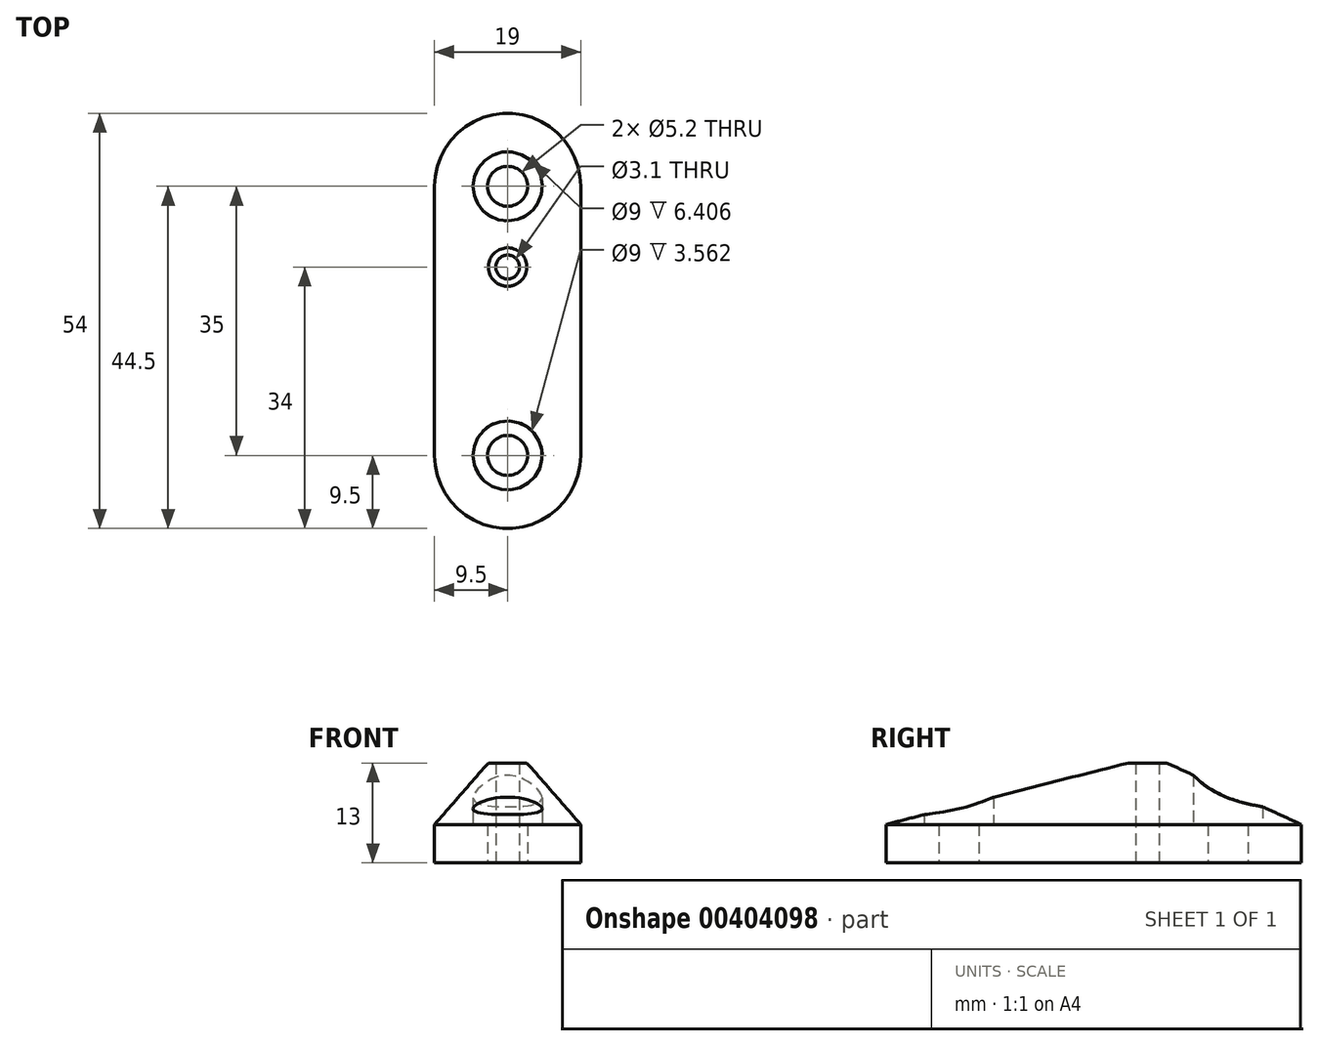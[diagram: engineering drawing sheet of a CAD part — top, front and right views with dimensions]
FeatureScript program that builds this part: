
annotation { "Feature Type Name" : "Feature", "Feature Type Description" : "" }
export const myFeature = defineFeature(function(context is Context, id is Id, definition is map)
    precondition{}
    {
        {
            var Q0;
            Q0=qCreatedBy(makeId("Top.planeOp"),FACE);
            var sketch = newSketch(context, id + "F0", { "sketchPlane" : qUnion([Q0])});
            skArc(sketch, "E0", {"start": v(9.5, 20) * mm, "mid": v(0, 29.5) * mm, "end": v(-9.5, 20) * mm});
            skArc(sketch, "E1", {"start": v(-9.5, -15) * mm, "mid": v(0, -24.5) * mm, "end": v(9.5, -15) * mm});
            skLineSegment(sketch, "E2", {"start": v(-9.5, 20) * mm, "end": v(-9.5, -15) * mm});
            skLineSegment(sketch, "E3", {"start": v(9.5, 20) * mm, "end": v(9.5, -15) * mm});
            skSolve(sketch);
        }
        {
            var Q0;
            Q0=makeQuery(id+"F0.imprint","IMPRINT",FACE,{"disambiguationData":[TD([[makeQuery(id+"F0.imprint","IMPRINT",EDGE,{"derivedFrom":sQuery(id+"F0.wireOp",EDGE,"E0")}),1.0]])]});
            extrude(context, id + "F1", {"entities" : qUnion([Q0]), "depth" : 5 * mm});
        }
        {
            var Q0;
            Q0=makeQuery(id+"F1.opExtrude","CAP_FACE",FACE,{"disambiguationData":[OSD([sQuery(id+"F0.wireOp",EDGE,"E0"),sQuery(id+"F0.wireOp",EDGE,"E1"),sQuery(id+"F0.wireOp",EDGE,"E2"),sQuery(id+"F0.wireOp",EDGE,"E3")])],"isStart":false});
            var sketch = newSketch(context, id + "F2", { "sketchPlane" : qUnion([Q0])});
            skCircle(sketch, "E4", {"center": v(0, -15) * mm, "radius": 4.5 * mm});
            skCircle(sketch, "E5", {"center": v(0, 20) * mm, "radius": 4.5 * mm});
            skSolve(sketch);
        }
        {
            var Q0;
            Q0=qCreatedBy(makeId("Top.planeOp"),FACE);
            cPlane(context, id + "F3", {"entities" : qUnion([Q0]), "cplaneType" : CPlaneType.OFFSET, "offset" : 13 * mm, "width" : 150 * mm, "height" : 150 * mm});
        }
        {
            var Q0;
            Q0=qCreatedBy(id+"F3.planeOp",FACE);
            var sketch = newSketch(context, id + "F4", { "sketchPlane" : qUnion([Q0])});
            skCircle(sketch, "E6", {"center": v(0, 9.5) * mm, "radius": 2.5 * mm});
            skSolve(sketch);
        }
        {
            var Q1;
            Q1=makeQuery(id+"F1.opExtrude","CAP_FACE",FACE,{"disambiguationData":[OSD([sQuery(id+"F0.wireOp",EDGE,"E0"),sQuery(id+"F0.wireOp",EDGE,"E1"),sQuery(id+"F0.wireOp",EDGE,"E2"),sQuery(id+"F0.wireOp",EDGE,"E3")])],"isStart":false});
            var Q2;
            Q2=makeQuery(id+"F4.imprint","IMPRINT",FACE,{"disambiguationData":[TD([[makeQuery(id+"F4.imprint","IMPRINT",EDGE,{"derivedFrom":sQuery(id+"F4.wireOp",EDGE,"E6")}),1.0]])]});
            loft(context, id + "F5", {"operationType" : NewBodyOperationType.ADD, "sheetProfilesArray" : [{ "sheetProfileEntities" : qUnion([Q1]) }, { "sheetProfileEntities" : qUnion([Q2]) }]});
        }
        {
            var Q0;
            Q0=makeQuery(id+"F1.opExtrude","CAP_FACE",FACE,{"disambiguationData":[OSD([sQuery(id+"F0.wireOp",EDGE,"E0"),sQuery(id+"F0.wireOp",EDGE,"E1"),sQuery(id+"F0.wireOp",EDGE,"E2"),sQuery(id+"F0.wireOp",EDGE,"E3")])],"isStart":true});
            var sketch = newSketch(context, id + "F6", { "sketchPlane" : qUnion([Q0])});
            skCircle(sketch, "E7", {"center": v(0, -9.5) * mm, "radius": 1.55 * mm});
            skCircle(sketch, "E8", {"center": v(0, 15) * mm, "radius": 2.6 * mm});
            skCircle(sketch, "E9", {"center": v(0, -20) * mm, "radius": 2.6 * mm});
            skSolve(sketch);
        }
        {
            var Q0;
            Q0=qSketchRegion(id+"F6",true);
            extrude(context, id + "F7", {"entities" : qUnion([Q0]), "operationType" : NewBodyOperationType.REMOVE, "oppositeDirection" : true, "depth" : 25 * mm});
        }
        {
            var Q0;
            Q0=qSketchRegion(id+"F2",true);
            extrude(context, id + "F8", {"entities" : qUnion([Q0]), "operationType" : NewBodyOperationType.REMOVE, "depth" : 25 * mm});
        }
    });
